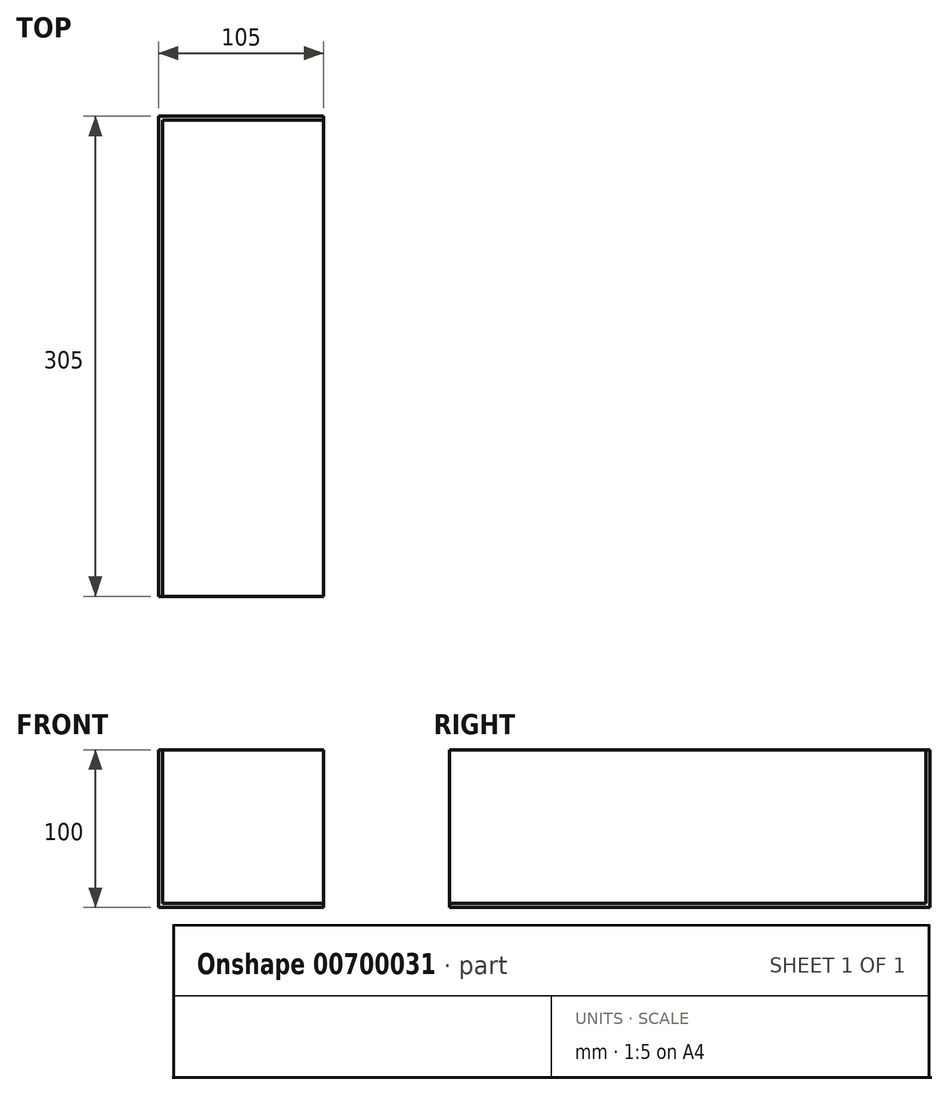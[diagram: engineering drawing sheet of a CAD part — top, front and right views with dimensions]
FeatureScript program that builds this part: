
annotation { "Feature Type Name" : "Feature", "Feature Type Description" : "" }
export const myFeature = defineFeature(function(context is Context, id is Id, definition is map)
    precondition{}
    {
        {
            var Q0;
            Q0=qCreatedBy(makeId("Top.planeOp"),FACE);
            var sketch = newSketch(context, id + "F0", { "sketchPlane" : qUnion([Q0])});
            skLineSegment(sketch, "E0.bottom", {"start": v(52.5, -152.5) * mm, "end": v(-52.5, -152.5) * mm});
            skLineSegment(sketch, "E0.top", {"start": v(52.5, 152.5) * mm, "end": v(-52.5, 152.5) * mm});
            skLineSegment(sketch, "E0.left", {"start": v(52.5, -152.5) * mm, "end": v(52.5, 152.5) * mm});
            skLineSegment(sketch, "E0.right", {"start": v(-52.5, -152.5) * mm, "end": v(-52.5, 152.5) * mm});
            skPoint(sketch, "E0.middle", {"position": v(0, 0) * mm});
            skSolve(sketch);
        }
        {
            var Q0;
            Q0=makeQuery(id+"F0.imprint","IMPRINT",FACE,{"disambiguationData":[TD([[makeQuery(id+"F0.imprint","IMPRINT",EDGE,{"derivedFrom":sQuery(id+"F0.wireOp",EDGE,"E0.bottom")}),-1.0]])]});
            extrude(context, id + "F1", {"entities" : qUnion([Q0]), "depth" : 100 * mm, "offsetDistance" : 25 * mm});
        }
        {
            var Q0;
            Q0=makeQuery(id+"F1.opExtrude","CAP_FACE",FACE,{"disambiguationData":[OSD([sQuery(id+"F0.wireOp",EDGE,"E0.bottom"),sQuery(id+"F0.wireOp",EDGE,"E0.top"),sQuery(id+"F0.wireOp",EDGE,"E0.left"),sQuery(id+"F0.wireOp",EDGE,"E0.right")])],"isStart":false});
            var Q1;
            Q1=makeQuery(id+"F1.opExtrude","SWEPT_FACE",FACE,{"disambiguationData":[OSD([sQuery(id+"F0.wireOp",EDGE,"E0.left")])]});
            var Q2;
            Q2=makeQuery(id+"F1.opExtrude","SWEPT_FACE",FACE,{"disambiguationData":[OSD([sQuery(id+"F0.wireOp",EDGE,"E0.bottom")])]});
            shell(context, id + "F2", {"entities" : qUnion([Q0, Q1, Q2]), "thickness" : 2.5 * mm});
        }
    });
